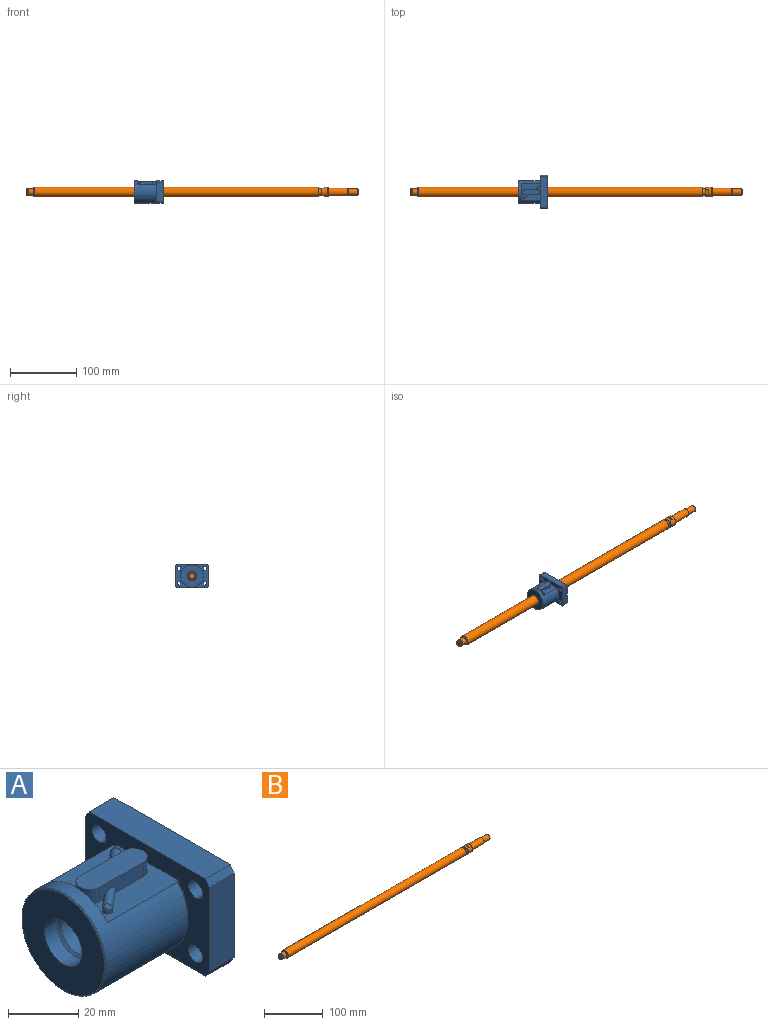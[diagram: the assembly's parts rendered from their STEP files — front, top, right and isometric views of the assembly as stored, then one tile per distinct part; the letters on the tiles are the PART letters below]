
ASSEMBLY  parts=2 mates=1
PART A: 52 faces, bbox 50.3x56.3x40.3 mm
  f0: cylinder r=2.46mm len=5.01mm, axis (1,0,0), area 77.3mm2, adj f1,f40,f47
  f1: cylinder r=2.5mm len=11.8mm, axis (0,-1,0), area 164.1mm2, adj f0,f9,f29,f34,f35,f36,f40,f43
  f2: cylinder r=7.5mm len=15mm, axis (1,0,0), area 235.6mm2, adj f38,f51
  f3: plane 9.5x9.5mm, normal (1,0,0), area 47.1mm2, adj f13,f16
  f4: plane 9.5x9.5mm, normal (1,0,0), area 47.1mm2, adj f11,f45
  f5: plane 9.5x9.5mm, normal (1,0,0), area 47.1mm2, adj f17,f44
  f6: plane 25.92x6mm, normal (1,0,0), area 108mm2, adj f12,f39
  f7: cylinder r=4mm len=8mm, axis (0,0,1), area 62.8mm2, adj f15,f31,f32,f39
  f8: plane 9.5x9.5mm, normal (1,0,0), area 47.1mm2, adj f18,f41
  f9: cylinder r=2.46mm len=4.92mm, axis (1,0,0), area 0.4mm2, adj f1,f29,f40
  f10: cone r=17mm half-angle=45deg, axis (1,0,0), area 50.8mm2, adj f12,f38
  f11: cylinder r=2.75mm len=5.5mm, axis (1,0,0), area 79.5mm2, adj f4,f20
  f12: cylinder r=17mm len=34mm, axis (1,0,0), area 2687.8mm2, adj f6,f10,f33,f39
  f13: cylinder r=4.75mm len=9.5mm, axis (-1,0,0), area 161.2mm2, adj f3,f37
  f14: cylinder r=29mm len=10mm, axis (1,0,0), area 27.5mm2, adj f20,f24,f25,f37
  f15: plane 25.5x8mm, normal (0,0,1), area 190.3mm2, adj f7,f31,f32,f42
  f16: cylinder r=2.75mm len=5.5mm, axis (1,0,0), area 79.5mm2, adj f3,f20
  f17: cylinder r=2.75mm len=5.5mm, axis (1,0,0), area 79.5mm2, adj f5,f20
  f18: cylinder r=2.75mm len=5.5mm, axis (1,0,0), area 79.5mm2, adj f8,f20
  f19: cylinder r=16.32mm len=32.64mm, axis (1,0,0), area 51.3mm2, adj f20,f33,f39
  f20: plane 50x34mm, normal (-1,0,0), area 850.3mm2, adj f11,f14,f16,f17,f18,f19,f21,f22
  f21: cylinder r=29mm len=10mm, axis (1,0,0), area 27.5mm2, adj f20,f22,f27,f37
  f22: plane 46.99x10mm, normal (0,0,1), area 469.9mm2, adj f20,f21,f23,f37
  f23: cylinder r=29mm len=10mm, axis (1,0,0), area 27.5mm2, adj f20,f22,f24,f37
  f24: plane 29.39x10mm, normal (0,-1,0), area 293.9mm2, adj f14,f20,f23,f37
  f25: plane 46.99x10mm, normal (0,0,-1), area 469.9mm2, adj f14,f20,f26,f37
  f26: cylinder r=29mm len=10mm, axis (1,0,0), area 27.5mm2, adj f20,f25,f27,f37
  f27: plane 29.39x10mm, normal (0,1,0), area 293.9mm2, adj f20,f21,f26,f37
  f28: cylinder r=1.5mm len=3mm, axis (0,0,-1), area 5.8mm2, adj f39,f49,f50
  f29: plane 11.24x8.99mm, normal (1,0,0), area 0.1mm2, adj f1,f9,f43
  f30: sphere r=1.5mm, area 7.1mm2, adj f46,f48
  f31: plane 18.65x6.15mm, normal (0,-1,0), area 77.7mm2, adj f7,f15,f39,f42,f49
  f32: plane 18.65x6.15mm, normal (0,1,0), area 77.7mm2, adj f7,f15,f39,f42,f46
  f33: plane 34x28mm, normal (1,0,0), area 51.9mm2, adj f12,f19,f39
  f34: cylinder r=7.5mm len=15mm, axis (1,0,0), area 235.6mm2, adj f1,f35,f37
  f35: cone r=7.5mm half-angle=45deg, axis (1,0,0), area 45.6mm2, adj f1,f34,f36
  f36: cylinder r=6.69mm len=32.38mm, axis (1,0,0), area 1349.5mm2, adj f1,f35,f51
  f37: plane 50x34mm, normal (1,0,0), area 1204.8mm2, adj f13,f14,f21,f22,f23,f24,f25,f26
  f38: plane 33.32x33.32mm, normal (-1,0,0), area 695.3mm2, adj f2,f10
  f39: plane 29x25.92mm, normal (0,0,1), area 518.3mm2, adj f6,f7,f12,f19,f20,f28,f31,f32
  f40: sphere r=2.5mm, area 7.1mm2, adj f0,f1,f9
  f41: cylinder r=4.75mm len=9.5mm, axis (-1,0,0), area 161.2mm2, adj f8,f37
  f42: cylinder r=4mm len=8mm, axis (0,0,1), area 62.8mm2, adj f15,f31,f32,f39
  f43: sphere r=2.5mm, area 0mm2, adj f1,f29
  f44: cylinder r=4.75mm len=9.5mm, axis (-1,0,0), area 161.2mm2, adj f5,f37
  f45: cylinder r=4.75mm len=9.5mm, axis (-1,0,0), area 161.2mm2, adj f4,f37
  f46: cylinder r=1.5mm len=9.1mm, axis (0.77,0.64,0), area 51.2mm2, adj f30,f32,f39,f48
  f47: cone r=3mm half-angle=45deg, axis (1,0,0), area 13.1mm2, adj f0,f37
  f48: cylinder r=1.5mm len=3mm, axis (0,0,-1), area 5.8mm2, adj f30,f39,f46
  f49: cylinder r=1.5mm len=9.1mm, axis (0.77,0.64,0), area 51.2mm2, adj f28,f31,f39,f50
  f50: sphere r=1.5mm, area 7.1mm2, adj f28,f49
  f51: cone r=6.69mm half-angle=45deg, axis (-1,0,0), area 51.2mm2, adj f2,f36
PART B: 28 faces, bbox 500x15x15 mm
  f0: cone r=4.5mm half-angle=45deg, axis (1,0,0), area 21.1mm2, adj f2,f27
  f1: cylinder r=4.8mm len=9.6mm, axis (1,0,0), area 34.7mm2, adj f3,f21
  f2: cylinder r=5mm len=10mm, axis (1,0,0), area 73.8mm2, adj f0,f21
  f3: plane 10x10mm, normal (-1,0,0), area 6.2mm2, adj f1,f26
  f4: cone r=7mm half-angle=45deg, axis (1,0,0), area 32.2mm2, adj f19,f25
  f5: cylinder r=5mm len=14.5mm, axis (1,0,0), area 455.5mm2, adj f11,f15
  f6: plane 15x15mm, normal (1,0,0), area 98.2mm2, adj f24,f25
  f7: plane 9x5mm, normal (0,0,-1), area 45mm2, adj f13,f14,f22
  f8: cylinder r=6mm len=29.2mm, axis (1,0,0), area 1100.8mm2, adj f9,f17
  f9: torus R=6.3mm, axis (-1,0,0), area 18.1mm2, adj f8,f12
  f10: plane 9x1.5mm, normal (-1,0,0), area 9.2mm2, adj f14,f23
  f11: cone r=4.5mm half-angle=45deg, axis (-1,0,0), area 21.1mm2, adj f5,f16
  f12: plane 14.6x14.6mm, normal (1,0,0), area 42.7mm2, adj f9,f20
  f13: plane 15x12mm, normal (-1,0,0), area 79.8mm2, adj f7,f14,f23,f24
  f14: cylinder r=7.5mm len=15mm, axis (1,0,0), area 365.3mm2, adj f7,f10,f13,f20,f22,f23
  f15: plane 11x11mm, normal (1,0,0), area 16.5mm2, adj f5,f17
  f16: plane 9x9mm, normal (1,0,0), area 63.6mm2, adj f11
  f17: cone r=5.5mm half-angle=45deg, axis (-1,0,0), area 25.5mm2, adj f8,f15
  f18: torus R=5.3mm, axis (-1,0,0), area 15.1mm2, adj f19,f26
  f19: plane 14x14mm, normal (-1,0,0), area 65.7mm2, adj f4,f18
  f20: cone r=7.3mm half-angle=45deg, axis (-1,0,0), area 13.2mm2, adj f12,f14
  f21: plane 10x10mm, normal (1,0,0), area 6.2mm2, adj f1,f2
  f22: plane 9x1.5mm, normal (-1,0,0), area 9.2mm2, adj f7,f14
  f23: plane 9x5mm, normal (0,0,1), area 45mm2, adj f10,f13,f14
  f24: cylinder r=5mm len=10mm, axis (1,0,0), area 157.1mm2, adj f6,f13
  f25: cylinder r=7.5mm len=427.5mm, axis (1,0,0), area 20145.5mm2, adj f4,f6
  f26: cylinder r=5mm len=10mm, axis (1,0,0), area 241.9mm2, adj f3,f18
  f27: plane 9x9mm, normal (-1,0,0), area 63.6mm2, adj f0
PLACE A t=(162.8,-3.36,0.97)mm
PLACE B t=(0,-3.36,0.97)mm
MATE cylindrical A.f2 <-> B.f0  axis (1,0,0) through (206.8,-3.36,0.97)mm
